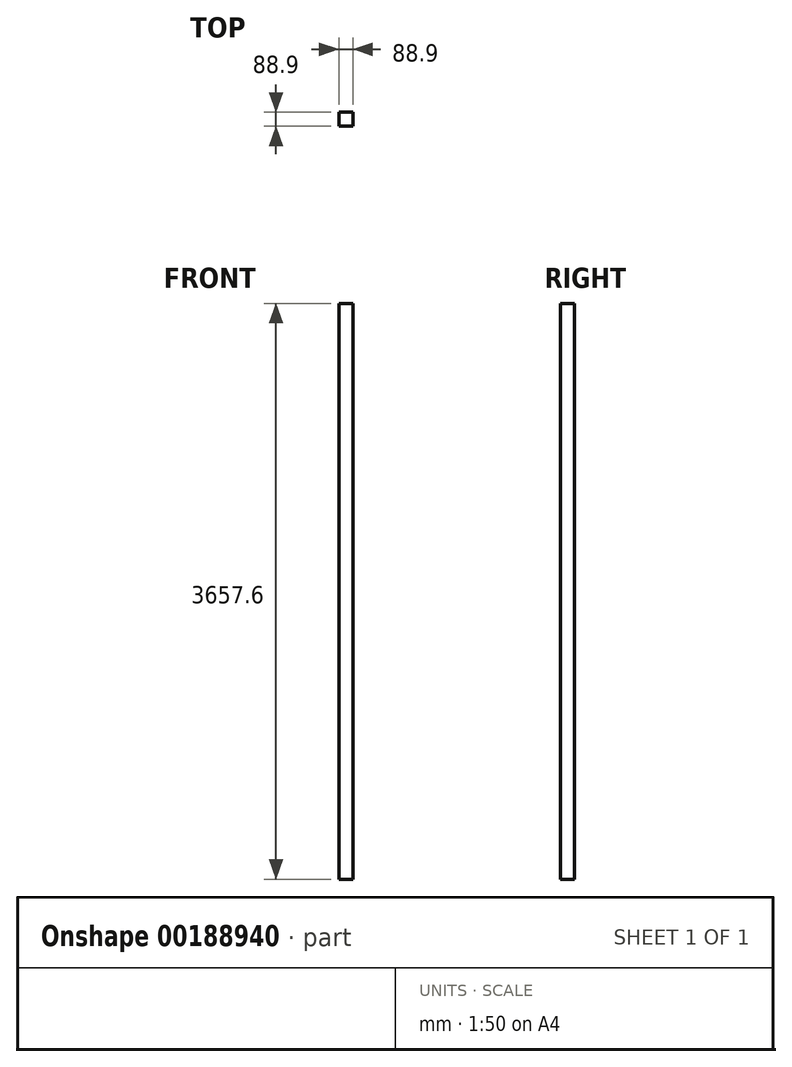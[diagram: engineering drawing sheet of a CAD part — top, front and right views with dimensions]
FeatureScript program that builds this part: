
annotation { "Feature Type Name" : "Feature", "Feature Type Description" : "" }
export const myFeature = defineFeature(function(context is Context, id is Id, definition is map)
    precondition{}
    {
        {
            var Q0;
            Q0=qCreatedBy(makeId("Top.planeOp"),FACE);
            var sketch = newSketch(context, id + "F1", { "sketchPlane" : qUnion([Q0])});
            skLineSegment(sketch, "E0.bottom", {"start": v(44.45, -44.45) * mm, "end": v(-44.45, -44.45) * mm});
            skLineSegment(sketch, "E0.top", {"start": v(44.45, 44.45) * mm, "end": v(-44.45, 44.45) * mm});
            skLineSegment(sketch, "E0.left", {"start": v(44.45, -44.45) * mm, "end": v(44.45, 44.45) * mm});
            skLineSegment(sketch, "E0.right", {"start": v(-44.45, -44.45) * mm, "end": v(-44.45, 44.45) * mm});
            skPoint(sketch, "E0.middle", {"position": v(0, 0) * mm});
            skSolve(sketch);
        }
        {
            var Q0;
            Q0=makeQuery(id+"F1.imprint","IMPRINT",FACE,{"disambiguationData":[TD([[makeQuery(id+"F1.imprint","IMPRINT",EDGE,{"derivedFrom":sQuery(id+"F1.wireOp",EDGE,"E0.bottom")}),-1.0]])]});
            extrude(context, id + "F0", {"entities" : qUnion([Q0]), "endBound" : BoundingType.SYMMETRIC, "depth" : 3657.6 * mm});
        }
    });
